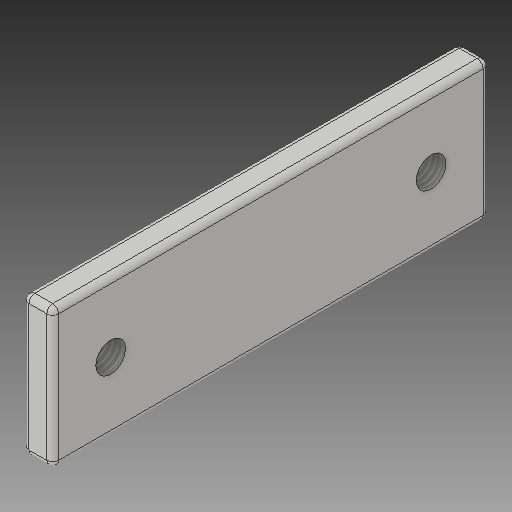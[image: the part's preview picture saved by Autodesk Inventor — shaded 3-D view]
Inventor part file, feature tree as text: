
AUTODESK INVENTOR PART (.ipt)
format: ipt  version: 2019 (Build 230136000, 136)  size: 123,904 bytes
history: native  units: in
note: dims shown in document units (in); Inventor stores cm internally (conversion verified against a paired STEP export)
features: extrude x2, sketch x2, thread x1, mirror x1, fillet x1
ambient origin geometry x8: Origin, YZ Plane, XZ Plane, XY Plane, X Axis, Y Axis, Z Axis, Center Point
bodies: Solid1 (feature_tree)
feature tree (7):
  extrude  "Extrusion1"  Depth=0.5512in
  extrude  "Extrusion2"  Depth=0.0236in
  thread  "Thread1"  [1 undecoded]
  mirror  "Mirror1"
  fillet  "Fillet1"  Radius=0.1181in
  sketch  "Sketch1"  dims[d0=1.7323in d1=0.5512in]
  sketch  "Sketch2"  dims[d2=0.1181in d3=0.0in d4=0.636in d5=0.1181in d6=0.1181in d7=0.0in d8=0.3937in d9=0.0in d10=0.0236in]
note: 1 required parameter value undecoded (feature->parameter linkage not recoverable at this tier; creation-order binding heuristic only, values carry confidence <= 0.55)
